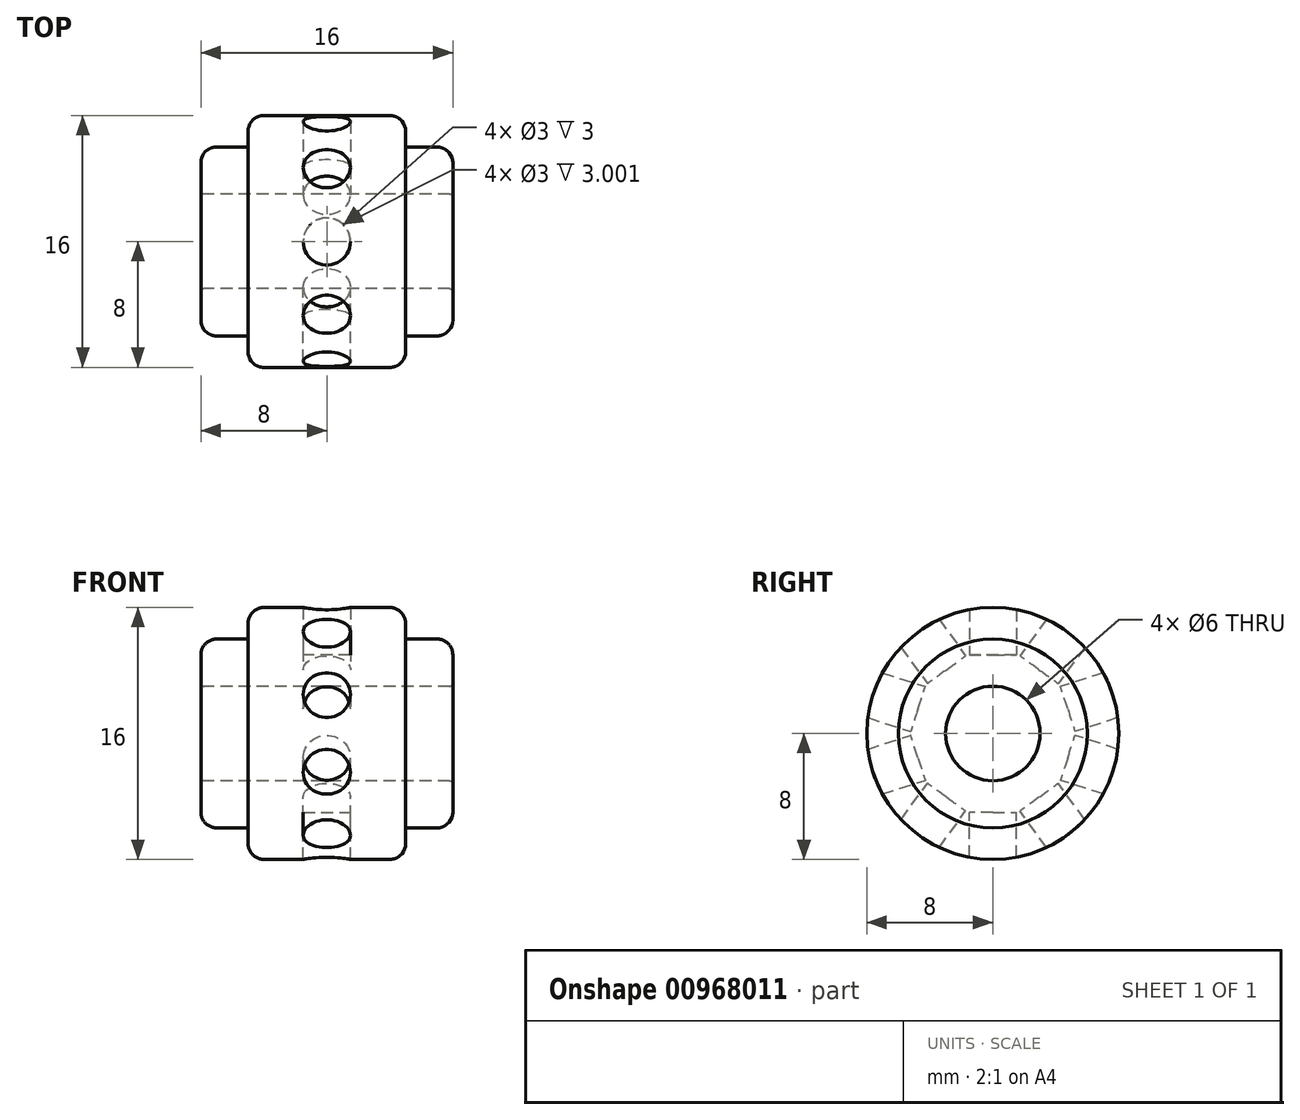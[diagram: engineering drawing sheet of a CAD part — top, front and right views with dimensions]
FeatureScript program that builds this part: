
annotation { "Feature Type Name" : "Feature", "Feature Type Description" : "" }
export const myFeature = defineFeature(function(context is Context, id is Id, definition is map)
    precondition{}
    {
        {
            var Q0;
            Q0=qCreatedBy(makeId("Front.planeOp"),FACE);
            var sketch = newSketch(context, id + "F0", { "sketchPlane" : qUnion([Q0])});
            skLineSegment(sketch, "E0", {"start": v(0, 3.2) * mm, "end": v(0, 5) * mm});
            skLineSegment(sketch, "E1", {"start": v(1, 6) * mm, "end": v(3, 6) * mm});
            skLineSegment(sketch, "E2", {"start": v(3, 6) * mm, "end": v(3, 7) * mm});
            skLineSegment(sketch, "E3", {"start": v(4, 8) * mm, "end": v(12, 8) * mm});
            skLineSegment(sketch, "E4", {"start": v(13, 7) * mm, "end": v(13, 6) * mm});
            skLineSegment(sketch, "E5", {"start": v(13, 6) * mm, "end": v(15, 6) * mm});
            skLineSegment(sketch, "E6", {"start": v(16, 5) * mm, "end": v(16, 3.2) * mm});
            skLineSegment(sketch, "E7", {"start": v(15.8, 3) * mm, "end": v(0.2, 3) * mm});
            skPoint(sketch, "E8.visualSharp", {"position": v(3, 8) * mm});
            skArc(sketch, "E8.filletArc", {"start": v(4, 8) * mm, "mid": v(3.3, 7.7) * mm, "end": v(3, 7) * mm});
            skPoint(sketch, "E9.visualSharp", {"position": v(13, 8) * mm});
            skArc(sketch, "E9.filletArc", {"start": v(13, 7) * mm, "mid": v(12.7, 7.7) * mm, "end": v(12, 8) * mm});
            skPoint(sketch, "E10.visualSharp", {"position": v(0, 6) * mm});
            skArc(sketch, "E10.filletArc", {"start": v(1, 6) * mm, "mid": v(0.3, 5.7) * mm, "end": v(0, 5) * mm});
            skPoint(sketch, "E11.visualSharp", {"position": v(16, 6) * mm});
            skArc(sketch, "E11.filletArc", {"start": v(16, 5) * mm, "mid": v(15.7, 5.7) * mm, "end": v(15, 6) * mm});
            skPoint(sketch, "E12.visualSharp", {"position": v(0, 3) * mm});
            skArc(sketch, "E12.filletArc", {"start": v(0, 3.2) * mm, "mid": v(0.06, 3.06) * mm, "end": v(0.2, 3) * mm});
            skPoint(sketch, "E13.visualSharp", {"position": v(16, 3) * mm});
            skArc(sketch, "E13.filletArc", {"start": v(15.8, 3) * mm, "mid": v(15.94, 3.06) * mm, "end": v(16, 3.2) * mm});
            skSolve(sketch);
        }
        {
            var Q0;
            Q0=qCreatedBy(makeId("Front.planeOp"),FACE);
            var sketch = newSketch(context, id + "F1", { "sketchPlane" : qUnion([Q0])});
            skLineSegment(sketch, "E14", {"start": v(0, 0) * mm, "end": v(18.15, 0) * mm});
            skSolve(sketch);
        }
        {
            var Q0;
            Q0=makeQuery(id+"F0.imprint","IMPRINT",FACE,{"disambiguationData":[TD([[makeQuery(id+"F0.imprint","IMPRINT",EDGE,{"derivedFrom":sQuery(id+"F0.wireOp",EDGE,"E0")}),-1.0]])]});
            var Q1;
            Q1=sQuery(id+"F1.wireOp",EDGE,"E14");
            revolve(context, id + "F2", {"surfaceOperationType" : NewSurfaceOperationType.NEW, "entities" : qUnion([Q0]), "axis" : qUnion([Q1]), "revolveType" : RevolveType.FULL});
        }
        {
            var Q0;
            Q0=makeQuery(id+"F2.opRevolve","SWEPT_BODY",BODY,{"disambiguationData":[OSD([sQuery(id+"F0.wireOp",EDGE,"E0"),sQuery(id+"F0.wireOp",EDGE,"E1"),sQuery(id+"F0.wireOp",EDGE,"E2"),sQuery(id+"F0.wireOp",EDGE,"E3"),sQuery(id+"F0.wireOp",EDGE,"E4"),sQuery(id+"F0.wireOp",EDGE,"E5"),sQuery(id+"F0.wireOp",EDGE,"E6"),sQuery(id+"F0.wireOp",EDGE,"E7"),sQuery(id+"F0.wireOp",EDGE,"E8.filletArc"),sQuery(id+"F0.wireOp",EDGE,"E9.filletArc"),sQuery(id+"F0.wireOp",EDGE,"E10.filletArc"),sQuery(id+"F0.wireOp",EDGE,"E11.filletArc"),sQuery(id+"F0.wireOp",EDGE,"E12.filletArc"),sQuery(id+"F0.wireOp",EDGE,"E13.filletArc")])]});
            transform(context, id + "F3", {"entities" : qUnion([Q0]), "transformType" : TransformType.TRANSLATION_3D, "dx" : -8 * mm, "dy" : 0 * mm, "dz" : 0 * mm, "makeCopy" : false});
        }
        {
            var Q0;
            Q0=qCreatedBy(makeId("Top.planeOp"),FACE);
            var sketch = newSketch(context, id + "F4", { "sketchPlane" : qUnion([Q0])});
            skCircle(sketch, "E15", {"center": v(0, 0) * mm, "radius": 1.5 * mm});
            skSolve(sketch);
        }
        {
            var Q0;
            Q0=makeQuery(id+"F4.imprint","IMPRINT",FACE,{"disambiguationData":[TD([[makeQuery(id+"F4.imprint","IMPRINT",EDGE,{"derivedFrom":sQuery(id+"F4.wireOp",EDGE,"E15")}),1.0]])]});
            extrude(context, id + "F5", {"entities" : qUnion([Q0]), "depth" : 10 * mm, "offsetDistance" : 25 * mm, "hasSecondDirection" : true, "secondDirectionOppositeDirection" : false, "secondDirectionDepth" : 5 * mm});
        }
        {
            var Q0;
            Q0=makeQuery(id+"F5.opExtrude","SWEPT_BODY",BODY,{"disambiguationData":[OSD([sQuery(id+"F4.wireOp",EDGE,"E15")])]});
            var Q1;
            Q1=makeQuery(id+"F2.opRevolve","SWEPT_FACE",FACE,{"disambiguationData":[OSD([sQuery(id+"F0.wireOp",EDGE,"E7")])]});
            circularPattern(context, id + "F6", {"operationType" : NewBodyOperationType.REMOVE, "entities" : qUnion([Q0]), "axis" : qUnion([Q1]), "angle" : 360 * degree, "instanceCount" : 10, "equalSpace" : true});
        }
    });
